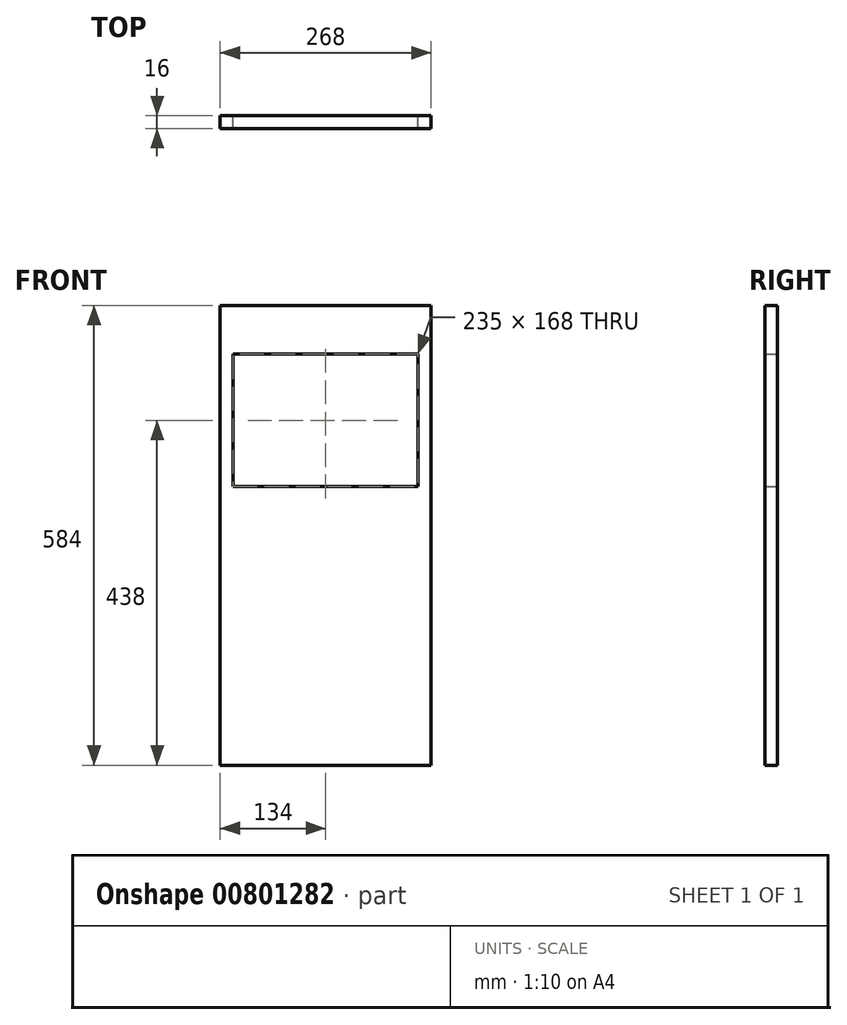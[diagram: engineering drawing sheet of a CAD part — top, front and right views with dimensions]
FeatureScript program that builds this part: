
annotation { "Feature Type Name" : "Feature", "Feature Type Description" : "" }
export const myFeature = defineFeature(function(context is Context, id is Id, definition is map)
    precondition{}
    {
        {
            var Q0;
            Q0=qCreatedBy(makeId("Front.planeOp"),FACE);
            var sketch = newSketch(context, id + "F0", { "sketchPlane" : qUnion([Q0])});
            skLineSegment(sketch, "E0.bottom", {"start": v(-134, -292) * mm, "end": v(134, -292) * mm});
            skLineSegment(sketch, "E0.top", {"start": v(-134, 292) * mm, "end": v(134, 292) * mm});
            skLineSegment(sketch, "E0.left", {"start": v(-134, -292) * mm, "end": v(-134, 292) * mm});
            skLineSegment(sketch, "E0.right", {"start": v(134, -292) * mm, "end": v(134, 292) * mm});
            skPoint(sketch, "E0.middle", {"position": v(0, 0) * mm});
            skLineSegment(sketch, "E1.bottom", {"start": v(127.5, 52) * mm, "end": v(-127.5, 52) * mm});
            skLineSegment(sketch, "E1.top", {"start": v(127.5, 240) * mm, "end": v(-127.5, 240) * mm});
            skLineSegment(sketch, "E1.left", {"start": v(127.5, 52) * mm, "end": v(127.5, 240) * mm});
            skLineSegment(sketch, "E1.right", {"start": v(-127.5, 52) * mm, "end": v(-127.5, 240) * mm});
            skPoint(sketch, "E1.middle", {"position": v(0, 146) * mm});
            skLineSegment(sketch, "E2.bottom", {"start": v(117.5, 62) * mm, "end": v(-117.5, 62) * mm});
            skLineSegment(sketch, "E2.top", {"start": v(117.5, 230) * mm, "end": v(-117.5, 230) * mm});
            skLineSegment(sketch, "E2.left", {"start": v(117.5, 62) * mm, "end": v(117.5, 230) * mm});
            skLineSegment(sketch, "E2.right", {"start": v(-117.5, 62) * mm, "end": v(-117.5, 230) * mm});
            skSolve(sketch);
        }
        {
            var Q0;
            Q0=makeQuery(id+"F0.imprint","IMPRINT",FACE,{"disambiguationData":[TD([[makeQuery(id+"F0.imprint","IMPRINT",EDGE,{"derivedFrom":sQuery(id+"F0.wireOp",EDGE,"E0.bottom")}),1.0]])]});
            var Q1;
            Q1=makeQuery(id+"F0.imprint","IMPRINT",FACE,{"disambiguationData":[TD([[makeQuery(id+"F0.imprint","IMPRINT",EDGE,{"derivedFrom":sQuery(id+"F0.wireOp",EDGE,"E1.bottom")}),-1.0]])]});
            extrude(context, id + "F1", {"entities" : qUnion([Q0, Q1]), "depth" : 16 * mm, "offsetDistance" : 25 * mm});
        }
    });
